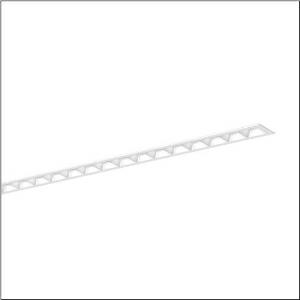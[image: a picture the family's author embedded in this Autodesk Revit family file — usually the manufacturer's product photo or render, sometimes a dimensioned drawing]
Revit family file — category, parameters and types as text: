
# Revit family: silica_r__21_51mx16dc4awb_037f
name_source: partatom
category: Lighting Fixtures
units: mm (PartAtom-declared; Revit-internal decimal feet)

## family parameters
Cut with Voids When Loaded = No
Host = Face
Light Source = No
Part Type = Normal
Room Calculation Point = No
Round Connector Dimension = Use Diameter
Shared = No

## types (1)
- --- (1 x LED, 10800 lm, 60.6 W, 4000K)
    Apparent Load = 61 VA
    CIE Flux Codes = 83 98 100 100 100
    Color Rendering = 80
    Color Temperature = 4000K
    Default Elevation = 1800 mm
    Description = Silica® 21, office luminaire, primary light control with darklight reflector, of PMMA, white, CAT 2 (L<= 3000cd/m²), light emission: direct distribution, primary light characteristic: symmetric, installation type: recessed, LED, rated luminous flux: 10.800lm, luminous efficacy: 178lm/W, light colour: 840, colour temperature: 4000K, control gear: DALI 2, with terminal, 3+2-pole, max. 2.5mm², mains connection: 220..240V, AC, 50/60Hz, rated input power: 60.6W, luminaire housing, of aluminium, traffic white (RAL 9016), length: 3.028mm, width: 79mm, height: 53mm, protection rating (complete): IP20, insulation class (complete): insulation class I (protective earthing), certification: CE, ENEC, VDE, permissible operating ambient temperature: 0..+35°C, standard: EN 50419, packaging unit: 1 piece
    Height = 0 mm  [stored 0 ft]
    Lamp = 1 x LED
    Lamp Light Flux = 10800 lm
    Lamp Power = 60.6 W
    Lamp count = 1
    Length = 3027 mm
    Luminous efficacy = 178 lm/W
    Manufacturer = Siteco
    ModVariant = No
    Model = 51MX16DC4AWB
    Mounting Place = Ceiling
    Mounting Type = Recessed
    Number of Poles = 1
    OnlyDefault = Yes
    Power Factor = 1
    Product Name = Silica® 21
    Product group = office luminaire | ceiling recessed
    ProductGroupID = 401
    Protection Class = Protection class I
    Protection Degree = IP 20
    RLX_Detail_Level = 1
    RLX_Emergency_Light_Flux = 0 lm
    RLX_Emergency_Type = 0
    RLX_Emergency_Type_DB = No
    RlxData = <blob elided: 60737 chars, md5=9b1a98c5>
    Socket = socket
    Standby Power = 0 W
    System Light Flux = 10800 lm
    System Power = 61 W
    Type Comments = factory setting: luminous flux: 100 % | dim-lin: 254 | 336 mA
    Type Image = l_1335884.jpg
    URL = http://relux.com
    VarID = @adj_124042
    Voltage = 0 V
    Weight = 0.00 kg
    Width = 79 mm

note: [stored X ft] marks values corroborated as IEEE doubles in the binary element streams (Revit-internal decimal feet)

## geometry (parser evidence)
native form markers: Blend x4, Sweep x13
no freeform markers — native parametric forms only
